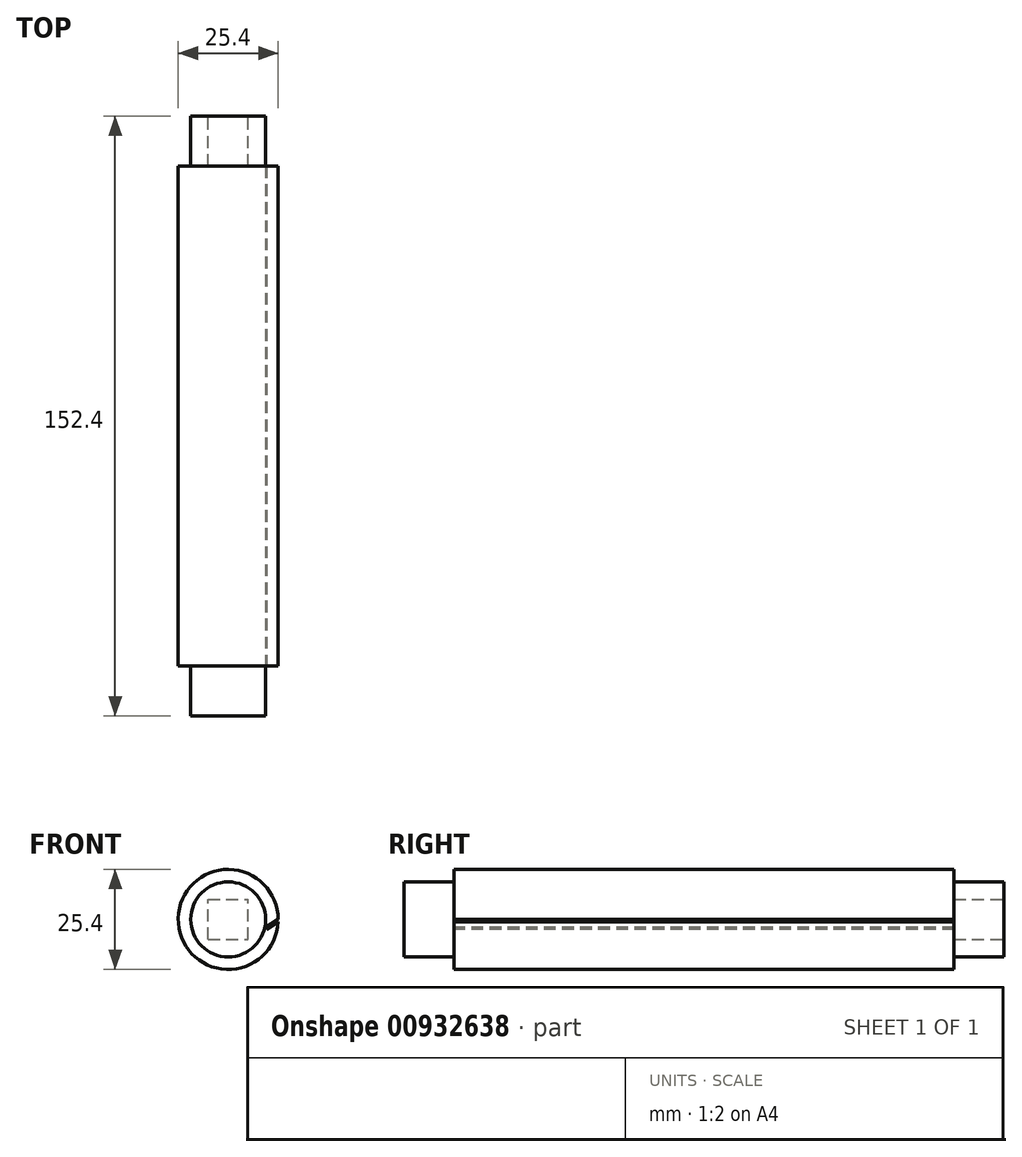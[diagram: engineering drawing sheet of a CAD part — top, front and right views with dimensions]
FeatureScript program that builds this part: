
annotation { "Feature Type Name" : "Feature", "Feature Type Description" : "" }
export const myFeature = defineFeature(function(context is Context, id is Id, definition is map)
    precondition{}
    {
        {
            var Q0;
            Q0=qCreatedBy(makeId("Front.planeOp"),FACE);
            var sketch = newSketch(context, id + "F0", { "sketchPlane" : qUnion([Q0])});
            skCircle(sketch, "E0", {"center": v(0, 0) * mm, "radius": 12.7 * mm});
            skLineSegment(sketch, "E1.bottom", {"start": v(5.08, -5.08) * mm, "end": v(-5.08, -5.08) * mm});
            skLineSegment(sketch, "E1.top", {"start": v(5.08, 5.08) * mm, "end": v(-5.08, 5.08) * mm});
            skLineSegment(sketch, "E1.left", {"start": v(5.08, -5.08) * mm, "end": v(5.08, 5.08) * mm});
            skLineSegment(sketch, "E1.right", {"start": v(-5.08, -5.08) * mm, "end": v(-5.08, 5.08) * mm});
            skCircle(sketch, "E2", {"center": v(0, 0) * mm, "radius": 9.53 * mm});
            skSolve(sketch);
        }
        {
            var Q0;
            Q0=makeQuery(id+"F0.imprint","IMPRINT",FACE,{"disambiguationData":[TD([[makeQuery(id+"F0.imprint","IMPRINT",EDGE,{"derivedFrom":sQuery(id+"F0.wireOp",EDGE,"E1.bottom")}),-1.0]])]});
            var Q1;
            Q1=makeQuery(id+"F0.imprint","IMPRINT",FACE,{"disambiguationData":[TD([[makeQuery(id+"F0.imprint","IMPRINT",EDGE,{"derivedFrom":sQuery(id+"F0.wireOp",EDGE,"E1.bottom")}),1.0]])]});
            var Q2;
            Q2=makeQuery(id+"F0.imprint","IMPRINT",FACE,{"disambiguationData":[TD([[makeQuery(id+"F0.imprint","IMPRINT",EDGE,{"derivedFrom":sQuery(id+"F0.wireOp",EDGE,"E0")}),1.0]])]});
            extrude(context, id + "F1", {"entities" : qUnion([Q0, Q1, Q2]), "depth" : 127 * mm, "offsetDistance" : 25.4 * mm});
        }
        {
            var Q0;
            Q0=makeQuery(id+"F0.imprint","IMPRINT",FACE,{"disambiguationData":[TD([[makeQuery(id+"F0.imprint","IMPRINT",EDGE,{"derivedFrom":sQuery(id+"F0.wireOp",EDGE,"E1.bottom")}),-1.0]])]});
            var Q1;
            Q1=makeQuery(id+"F0.imprint","IMPRINT",FACE,{"disambiguationData":[TD([[makeQuery(id+"F0.imprint","IMPRINT",EDGE,{"derivedFrom":sQuery(id+"F0.wireOp",EDGE,"E1.bottom")}),1.0]])]});
            extrude(context, id + "F2", {"entities" : qUnion([Q0, Q1]), "operationType" : NewBodyOperationType.ADD, "oppositeDirection" : true, "depth" : 12.7 * mm, "offsetDistance" : 25.4 * mm});
        }
        {
            var Q0;
            Q0=makeQuery(id+"F2.opExtrude","CAP_FACE",FACE,{"disambiguationData":[OSD([sQuery(id+"F0.wireOp",EDGE,"E2")])],"isStart":false});
            var sketch = newSketch(context, id + "F3", { "sketchPlane" : qUnion([Q0])});
            skLineSegment(sketch, "E3.bottom", {"start": v(5.08, -5.08) * mm, "end": v(-5.08, -5.08) * mm});
            skLineSegment(sketch, "E3.top", {"start": v(5.08, 5.08) * mm, "end": v(-5.08, 5.08) * mm});
            skLineSegment(sketch, "E3.left", {"start": v(5.08, -5.08) * mm, "end": v(5.08, 5.08) * mm});
            skLineSegment(sketch, "E3.right", {"start": v(-5.08, -5.08) * mm, "end": v(-5.08, 5.08) * mm});
            skPoint(sketch, "E3.middle", {"position": v(0, 0) * mm});
            skSolve(sketch);
        }
        {
            var Q0;
            Q0=makeQuery(id+"F3.imprint","IMPRINT",FACE,{"disambiguationData":[TD([[makeQuery(id+"F3.imprint","IMPRINT",EDGE,{"derivedFrom":sQuery(id+"F3.wireOp",EDGE,"E3.bottom")}),-1.0]])]});
            extrude(context, id + "F4", {"entities" : qUnion([Q0]), "operationType" : NewBodyOperationType.REMOVE, "oppositeDirection" : true, "depth" : 12.7 * mm, "offsetDistance" : 25.4 * mm});
        }
        {
            var Q0;
            Q0=makeQuery(id+"F1.opExtrude","CAP_FACE",FACE,{"disambiguationData":[OSD([sQuery(id+"F0.wireOp",EDGE,"E0")])],"isStart":false});
            var sketch = newSketch(context, id + "F5", { "sketchPlane" : qUnion([Q0])});
            skCircle(sketch, "E4", {"center": v(0, 0) * mm, "radius": 9.53 * mm});
            skSolve(sketch);
        }
        {
            var Q0;
            Q0=makeQuery(id+"F5.imprint","IMPRINT",FACE,{"disambiguationData":[TD([[makeQuery(id+"F5.imprint","IMPRINT",EDGE,{"derivedFrom":sQuery(id+"F5.wireOp",EDGE,"E4")}),1.0]])]});
            extrude(context, id + "F6", {"entities" : qUnion([Q0]), "operationType" : NewBodyOperationType.ADD, "depth" : 12.7 * mm, "offsetDistance" : 25.4 * mm});
        }
        {
            var Q0;
            Q0=makeQuery(id+"F1.opExtrude","CAP_FACE",FACE,{"disambiguationData":[OSD([sQuery(id+"F0.wireOp",EDGE,"E0")])],"isStart":false});
            var sketch = newSketch(context, id + "F7", { "sketchPlane" : qUnion([Q0])});
            skLineSegment(sketch, "E5", {"start": v(0, 0) * mm, "end": v(12.7, 0) * mm});
            skLineSegment(sketch, "E6", {"start": v(12.7, 0) * mm, "end": v(9.48, -2.04) * mm});
            skLineSegment(sketch, "E7", {"start": v(9.76, -2.47) * mm, "end": v(9.48, -2.04) * mm});
            skLineSegment(sketch, "E8", {"start": v(9.76, -2.47) * mm, "end": v(14.76, 0.7) * mm});
            skLineSegment(sketch, "E9", {"start": v(14.76, 0.7) * mm, "end": v(14.49, 1.14) * mm});
            skLineSegment(sketch, "E10", {"start": v(12.7, 0) * mm, "end": v(14.49, 1.14) * mm});
            skSolve(sketch);
        }
        {
            var Q0;
            Q0 = qSketchRegion(id + "F7", true);
            extrude(context, id + "F8", {"entities" : qUnion([Q0]), "operationType" : NewBodyOperationType.REMOVE, "endBound" : BoundingType.THROUGH_ALL, "oppositeDirection" : true, "depth" : 25.4 * mm, "offsetDistance" : 25.4 * mm});
        }
    });
